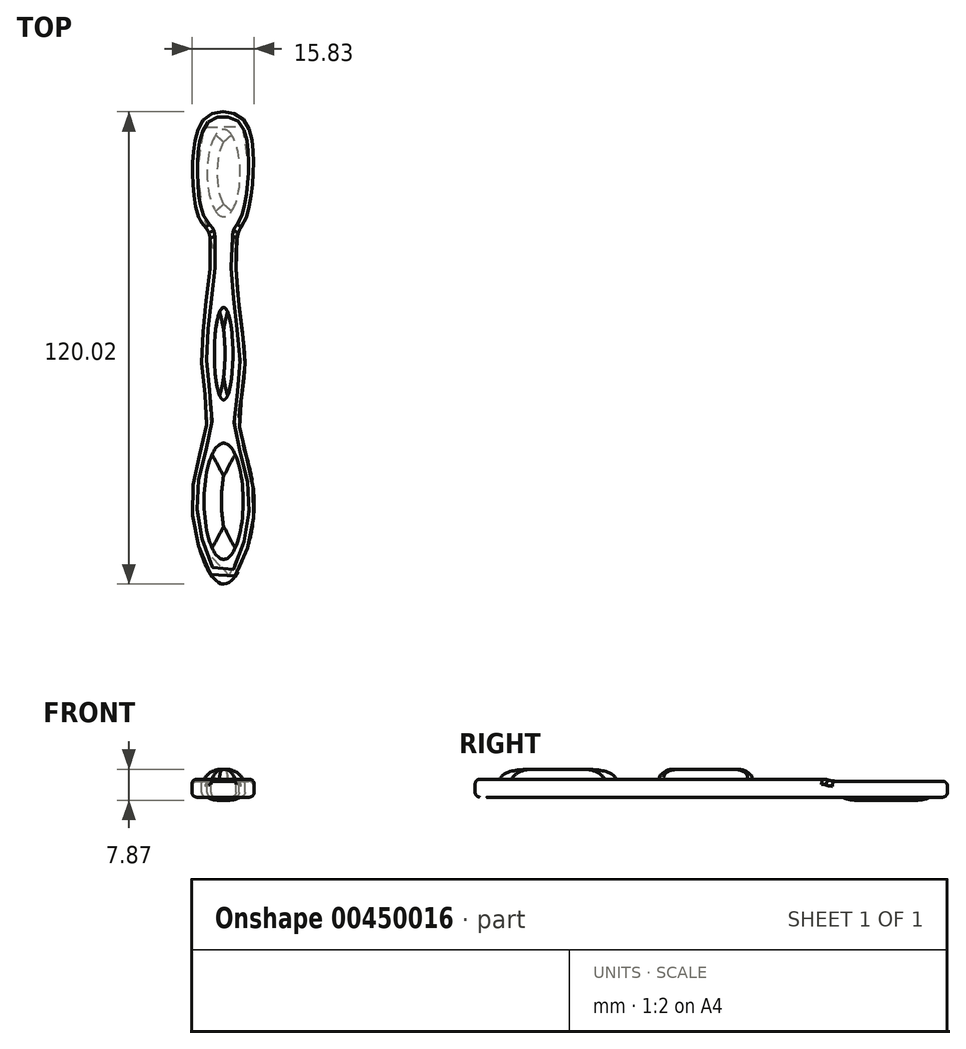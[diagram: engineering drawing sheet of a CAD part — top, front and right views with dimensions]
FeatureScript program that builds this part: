
annotation { "Feature Type Name" : "Feature", "Feature Type Description" : "" }
export const myFeature = defineFeature(function(context is Context, id is Id, definition is map)
    precondition{}
    {
        {
            var Q0;
            Q0=qCreatedBy(makeId("Top.planeOp"),FACE);
            var sketch = newSketch(context, id + "F0", { "sketchPlane" : qUnion([Q0])});
            skFitSpline(sketch, "E0", {"points": [v(-6.33, 25.61) * mm, v(-3.74, 21.59) * mm, v(-4.32, 5.18) * mm, v(-5.47, -13.81) * mm, v(-4.32, -27.34) * mm, v(-8.06, -46.91) * mm, v(0, -67.63) * mm, v(7.77, -47.49) * mm, v(4.03, -27.63) * mm, v(5.35, -13.96) * mm, v(3.74, 4.9) * mm, v(3.74, 21.59) * mm, v(5.76, 25.61) * mm, v(6.33, 48.35) * mm, v(0, 52.38) * mm, v(-6.24, 48.59) * mm, v(-6.33, 25.61) * mm]});
            skSolve(sketch);
        }
        {
            var Q0;
            Q0=makeQuery(id+"F0.imprint","IMPRINT",FACE,{"disambiguationData":[TD([[makeQuery(id+"F0.imprint","IMPRINT",EDGE,{"derivedFrom":sQuery(id+"F0.wireOp",EDGE,"E0")}),1.0]])]});
            var sketch = newSketch(context, id + "F1", { "sketchPlane" : qUnion([Q0])});
            skLineSegment(sketch, "E1", {"start": v(3.74, 21.59) * mm, "end": v(-3.74, 21.59) * mm});
            skSolve(sketch);
        }
        {
            var Q0;
            Q0=makeQuery(id+"F0.imprint","IMPRINT",FACE,{"disambiguationData":[TD([[makeQuery(id+"F0.imprint","IMPRINT",EDGE,{"derivedFrom":sQuery(id+"F0.wireOp",EDGE,"E0")}),1.0]])]});
            extrude(context, id + "F2", {"entities" : qUnion([Q0]), "depth" : 4.06 * mm});
        }
        {
            var Q0;
            {var subQ0=sQuery(id+"F1.wireOp",EDGE,"E1");var subQ1=makeQuery(id+"F0.imprint","IMPRINT",EDGE,{"derivedFrom":sQuery(id+"F0.wireOp",EDGE,"E0")});var subQ2=makeQuery(id+"F1.imprint","INTERSECT",VERTEX,{"disambiguationData":[OD(0.0)],"derivedFrom":[subQ1,subQ0]});Q0=makeQuery(id+"F1.imprint","IMPRINT",FACE,{"disambiguationData":[TD([[makeQuery(id+"F1.imprint","IMPRINT",EDGE,{"disambiguationData":[TD([[subQ2,1.0]])],"derivedFrom":subQ0}),-1.0]])]});}
            var sketch = newSketch(context, id + "F3", { "sketchPlane" : qUnion([Q0])});
            skLineSegment(sketch, "E2", {"start": v(-3.74, 21.59) * mm, "end": v(3.74, 21.59) * mm});
            skSolve(sketch);
        }
        {
            var Q0;
            {var subQ0=sQuery(id+"F1.wireOp",EDGE,"E1");var subQ1=makeQuery(id+"F0.imprint","IMPRINT",EDGE,{"derivedFrom":sQuery(id+"F0.wireOp",EDGE,"E0")});var subQ2=makeQuery(id+"F1.imprint","INTERSECT",VERTEX,{"disambiguationData":[OD(0.0)],"derivedFrom":[subQ1,subQ0]});Q0=makeQuery(id+"F1.imprint","IMPRINT",FACE,{"disambiguationData":[TD([[makeQuery(id+"F1.imprint","IMPRINT",EDGE,{"disambiguationData":[TD([[subQ2,1.0]])],"derivedFrom":subQ0}),1.0]])]});}
            extrude(context, id + "F4", {"entities" : qUnion([Q0]), "operationType" : NewBodyOperationType.ADD, "depth" : 4.57 * mm});
        }
        {
            var Q0;
            Q0=makeQuery(id+"F4.boolean.opBoolean","INTERSECT",EDGE,{"derivedFrom":[makeQuery(id+"F2.opExtrude","CAP_FACE",FACE,{"disambiguationData":[OSD([sQuery(id+"F0.wireOp",EDGE,"E0")])],"isStart":false}),makeQuery(id+"F4.opExtrude","SWEPT_FACE",FACE,{"disambiguationData":[OSD([sQuery(id+"F1.wireOp",EDGE,"E1")])]})]});
            fillet(context, id + "F5", {"entities" : qUnion([Q0]), "radius" : 5.08 * mm, "tangentPropagation" : true, "allowEdgeOverflow" : false});
        }
        {
            var Q0;
            {var subQ0=sQuery(id+"F1.wireOp",EDGE,"E1");var subQ1=sQuery(id+"F0.wireOp",EDGE,"E0");Q0=makeQuery(id+"F5.opFillet","BLEND_EDGE",EDGE,{"blendedFrom":[makeQuery(id+"F4.boolean.opBoolean","INTERSECT",EDGE,{"derivedFrom":[makeQuery(id+"F2.opExtrude","CAP_FACE",FACE,{"disambiguationData":[OSD([subQ1])],"isStart":false}),makeQuery(id+"F4.opExtrude","SWEPT_FACE",FACE,{"disambiguationData":[OSD([subQ0])]})]}),makeQuery(id+"F4.opExtrude","CAP_FACE",FACE,{"disambiguationData":[OSD([subQ1,subQ0])],"isStart":false})],"blendedInto":[makeQuery(id+"F4.opExtrude","CAP_FACE",FACE,{"disambiguationData":[OSD([subQ1,subQ0])],"isStart":false})]});}
            fillet(context, id + "F6", {"entities" : qUnion([Q0]), "radius" : 5.08 * mm, "tangentPropagation" : true, "allowEdgeOverflow" : false});
        }
        {
            var Q0;
            Q0=makeQuery(id+"F2.opExtrude","CAP_EDGE",EDGE,{"disambiguationData":[OSD([sQuery(id+"F0.wireOp",EDGE,"E0")])],"isStart":false});
            var Q1;
            {var subQ0=sQuery(id+"F0.wireOp",EDGE,"E0");Q1=makeQuery(id+"F5.opFillet","BLEND_EDGE",EDGE,{"disambiguationData":[OD(1.0)],"blendedFrom":[makeQuery(id+"F4.boolean.opBoolean","INTERSECT",EDGE,{"derivedFrom":[makeQuery(id+"F2.opExtrude","CAP_FACE",FACE,{"disambiguationData":[OSD([subQ0])],"isStart":false}),makeQuery(id+"F4.opExtrude","SWEPT_FACE",FACE,{"disambiguationData":[OSD([sQuery(id+"F1.wireOp",EDGE,"E1")])]})]}),makeQuery(id+"F4.boolean.opBoolean","MERGE",FACE,{"derivedFrom":[makeQuery(id+"F2.opExtrude","SWEPT_FACE",FACE,{"disambiguationData":[OSD([subQ0])]}),makeQuery(id+"F4.opExtrude","SWEPT_FACE",FACE,{"disambiguationData":[OSD([subQ0])]})]})],"blendedInto":[makeQuery(id+"F4.boolean.opBoolean","MERGE",FACE,{"derivedFrom":[makeQuery(id+"F2.opExtrude","SWEPT_FACE",FACE,{"disambiguationData":[OSD([subQ0])]}),makeQuery(id+"F4.opExtrude","SWEPT_FACE",FACE,{"disambiguationData":[OSD([subQ0])]})]})]});}
            var Q2;
            {var subQ0=sQuery(id+"F0.wireOp",EDGE,"E0");var subQ1=sQuery(id+"F1.wireOp",EDGE,"E1");Q2=makeQuery(id+"F6.opFillet","BLEND_EDGE",EDGE,{"disambiguationData":[OD(1.0)],"blendedFrom":[makeQuery(id+"F5.opFillet","BLEND_EDGE",EDGE,{"blendedFrom":[makeQuery(id+"F4.boolean.opBoolean","INTERSECT",EDGE,{"derivedFrom":[makeQuery(id+"F2.opExtrude","CAP_FACE",FACE,{"disambiguationData":[OSD([subQ0])],"isStart":false}),makeQuery(id+"F4.opExtrude","SWEPT_FACE",FACE,{"disambiguationData":[OSD([subQ1])]})]}),makeQuery(id+"F4.opExtrude","CAP_FACE",FACE,{"disambiguationData":[OSD([subQ0,subQ1])],"isStart":false})],"blendedInto":[makeQuery(id+"F4.opExtrude","CAP_FACE",FACE,{"disambiguationData":[OSD([subQ0,subQ1])],"isStart":false})]}),makeQuery(id+"F4.boolean.opBoolean","MERGE",FACE,{"derivedFrom":[makeQuery(id+"F2.opExtrude","SWEPT_FACE",FACE,{"disambiguationData":[OSD([subQ0])]}),makeQuery(id+"F4.opExtrude","SWEPT_FACE",FACE,{"disambiguationData":[OSD([subQ0])]})]})],"blendedInto":[makeQuery(id+"F4.boolean.opBoolean","MERGE",FACE,{"derivedFrom":[makeQuery(id+"F2.opExtrude","SWEPT_FACE",FACE,{"disambiguationData":[OSD([subQ0])]}),makeQuery(id+"F4.opExtrude","SWEPT_FACE",FACE,{"disambiguationData":[OSD([subQ0])]})]})]});}
            var Q3;
            Q3=makeQuery(id+"F4.opExtrude","CAP_EDGE",EDGE,{"disambiguationData":[OSD([sQuery(id+"F0.wireOp",EDGE,"E0")])],"isStart":false});
            var Q4;
            {var subQ0=sQuery(id+"F0.wireOp",EDGE,"E0");var subQ1=sQuery(id+"F1.wireOp",EDGE,"E1");Q4=makeQuery(id+"F6.opFillet","BLEND_EDGE",EDGE,{"disambiguationData":[OD(0.0)],"blendedFrom":[makeQuery(id+"F5.opFillet","BLEND_EDGE",EDGE,{"blendedFrom":[makeQuery(id+"F4.boolean.opBoolean","INTERSECT",EDGE,{"derivedFrom":[makeQuery(id+"F2.opExtrude","CAP_FACE",FACE,{"disambiguationData":[OSD([subQ0])],"isStart":false}),makeQuery(id+"F4.opExtrude","SWEPT_FACE",FACE,{"disambiguationData":[OSD([subQ1])]})]}),makeQuery(id+"F4.opExtrude","CAP_FACE",FACE,{"disambiguationData":[OSD([subQ0,subQ1])],"isStart":false})],"blendedInto":[makeQuery(id+"F4.opExtrude","CAP_FACE",FACE,{"disambiguationData":[OSD([subQ0,subQ1])],"isStart":false})]}),makeQuery(id+"F4.boolean.opBoolean","MERGE",FACE,{"derivedFrom":[makeQuery(id+"F2.opExtrude","SWEPT_FACE",FACE,{"disambiguationData":[OSD([subQ0])]}),makeQuery(id+"F4.opExtrude","SWEPT_FACE",FACE,{"disambiguationData":[OSD([subQ0])]})]})],"blendedInto":[makeQuery(id+"F4.boolean.opBoolean","MERGE",FACE,{"derivedFrom":[makeQuery(id+"F2.opExtrude","SWEPT_FACE",FACE,{"disambiguationData":[OSD([subQ0])]}),makeQuery(id+"F4.opExtrude","SWEPT_FACE",FACE,{"disambiguationData":[OSD([subQ0])]})]})]});}
            var Q5;
            {var subQ0=sQuery(id+"F0.wireOp",EDGE,"E0");Q5=makeQuery(id+"F5.opFillet","BLEND_EDGE",EDGE,{"disambiguationData":[OD(0.0)],"blendedFrom":[makeQuery(id+"F4.boolean.opBoolean","INTERSECT",EDGE,{"derivedFrom":[makeQuery(id+"F2.opExtrude","CAP_FACE",FACE,{"disambiguationData":[OSD([subQ0])],"isStart":false}),makeQuery(id+"F4.opExtrude","SWEPT_FACE",FACE,{"disambiguationData":[OSD([sQuery(id+"F1.wireOp",EDGE,"E1")])]})]}),makeQuery(id+"F4.boolean.opBoolean","MERGE",FACE,{"derivedFrom":[makeQuery(id+"F2.opExtrude","SWEPT_FACE",FACE,{"disambiguationData":[OSD([subQ0])]}),makeQuery(id+"F4.opExtrude","SWEPT_FACE",FACE,{"disambiguationData":[OSD([subQ0])]})]})],"blendedInto":[makeQuery(id+"F4.boolean.opBoolean","MERGE",FACE,{"derivedFrom":[makeQuery(id+"F2.opExtrude","SWEPT_FACE",FACE,{"disambiguationData":[OSD([subQ0])]}),makeQuery(id+"F4.opExtrude","SWEPT_FACE",FACE,{"disambiguationData":[OSD([subQ0])]})]})]});}
            fillet(context, id + "F7", {"entities" : qUnion([Q0, Q1, Q2, Q3, Q4, Q5]), "radius" : 1.27 * mm, "tangentPropagation" : true, "allowEdgeOverflow" : false});
        }
        {
            var Q0;
            Q0=makeQuery(id+"F2.opExtrude","CAP_EDGE",EDGE,{"disambiguationData":[OSD([sQuery(id+"F0.wireOp",EDGE,"E0")])],"isStart":true});
            fillet(context, id + "F8", {"entities" : qUnion([Q0]), "radius" : 1.27 * mm, "tangentPropagation" : true, "allowEdgeOverflow" : false});
        }
        {
            var Q0;
            {var subQ0=sQuery(id+"F1.wireOp",EDGE,"E1");var subQ1=makeQuery(id+"F0.imprint","IMPRINT",EDGE,{"derivedFrom":sQuery(id+"F0.wireOp",EDGE,"E0")});var subQ2=makeQuery(id+"F1.imprint","INTERSECT",VERTEX,{"disambiguationData":[OD(0.0)],"derivedFrom":[subQ1,subQ0]});Q0=makeQuery(id+"F3.imprint","IMPRINT",FACE,{"disambiguationData":[TD([[makeQuery(id+"F3.imprint","IMPRINT",EDGE,{"derivedFrom":makeQuery(id+"F1.imprint","IMPRINT",EDGE,{"disambiguationData":[TD([[subQ2,1.0]])],"derivedFrom":subQ0})}),-1.0]])]});}
            var sketch = newSketch(context, id + "F9", { "sketchPlane" : qUnion([Q0])});
            skEllipse(sketch, "E3", {"center": v(0, 36.82) * mm, "majorRadius": 11.08 * mm, "minorRadius": 4.2 * mm, "majorAxis": v(0, 1)});
            skSolve(sketch);
        }
        {
            var Q0;
            Q0=makeQuery(id+"F9.imprint","IMPRINT",FACE,{"disambiguationData":[TD([[makeQuery(id+"F9.imprint","IMPRINT",EDGE,{"derivedFrom":sQuery(id+"F9.wireOp",EDGE,"E3")}),1.0]])]});
            extrude(context, id + "F10", {"entities" : qUnion([Q0]), "operationType" : NewBodyOperationType.ADD, "oppositeDirection" : true, "depth" : 0.76 * mm});
        }
        {
            var Q0;
            Q0=makeQuery(id+"F10.opExtrude","CAP_EDGE",EDGE,{"disambiguationData":[OSD([sQuery(id+"F9.wireOp",EDGE,"E3")])],"isStart":false});
            fillet(context, id + "F11", {"entities" : qUnion([Q0]), "radius" : 5.08 * mm, "tangentPropagation" : true, "allowEdgeOverflow" : false});
        }
        {
            var Q0;
            Q0=makeQuery(id+"F4.opExtrude","CAP_FACE",FACE,{"disambiguationData":[OSD([sQuery(id+"F0.wireOp",EDGE,"E0"),sQuery(id+"F1.wireOp",EDGE,"E1")])],"isStart":false});
            var sketch = newSketch(context, id + "F12", { "sketchPlane" : qUnion([Q0])});
            skEllipse(sketch, "E4", {"center": v(0, -46.56) * mm, "majorRadius": 14.76 * mm, "minorRadius": 4.96 * mm, "majorAxis": v(0, -1)});
            skSolve(sketch);
        }
        {
            var Q0;
            Q0=makeQuery(id+"F12.imprint","IMPRINT",FACE,{"disambiguationData":[TD([[makeQuery(id+"F12.imprint","IMPRINT",EDGE,{"derivedFrom":sQuery(id+"F12.wireOp",EDGE,"E4")}),1.0]])]});
            extrude(context, id + "F13", {"entities" : qUnion([Q0]), "operationType" : NewBodyOperationType.ADD, "depth" : 2.54 * mm});
        }
        {
            var Q0;
            Q0=makeQuery(id+"F13.opExtrude","CAP_EDGE",EDGE,{"disambiguationData":[OSD([sQuery(id+"F12.wireOp",EDGE,"E4")])],"isStart":false});
            fillet(context, id + "F14", {"entities" : qUnion([Q0]), "radius" : 5.08 * mm, "tangentPropagation" : true, "allowEdgeOverflow" : false});
        }
        {
            var Q0;
            Q0=makeQuery(id+"F4.opExtrude","CAP_FACE",FACE,{"disambiguationData":[OSD([sQuery(id+"F0.wireOp",EDGE,"E0"),sQuery(id+"F1.wireOp",EDGE,"E1")])],"isStart":false});
            var sketch = newSketch(context, id + "F15", { "sketchPlane" : qUnion([Q0])});
            skEllipse(sketch, "E5", {"center": v(0, -9.07) * mm, "majorRadius": 11.74 * mm, "minorRadius": 2.36 * mm, "majorAxis": v(0, -1)});
            skSolve(sketch);
        }
        {
            var Q0;
            Q0=makeQuery(id+"F15.imprint","IMPRINT",FACE,{"disambiguationData":[TD([[makeQuery(id+"F15.imprint","IMPRINT",EDGE,{"derivedFrom":sQuery(id+"F15.wireOp",EDGE,"E5")}),1.0]])]});
            extrude(context, id + "F16", {"entities" : qUnion([Q0]), "operationType" : NewBodyOperationType.ADD, "depth" : 2.54 * mm});
        }
        {
            var Q0;
            Q0=makeQuery(id+"F16.opExtrude","CAP_FACE",FACE,{"disambiguationData":[OSD([sQuery(id+"F15.wireOp",EDGE,"E5")])],"isStart":false});
            fillet(context, id + "F17", {"entities" : qUnion([Q0]), "radius" : 2.03 * mm, "tangentPropagation" : true, "allowEdgeOverflow" : false});
        }
    });
